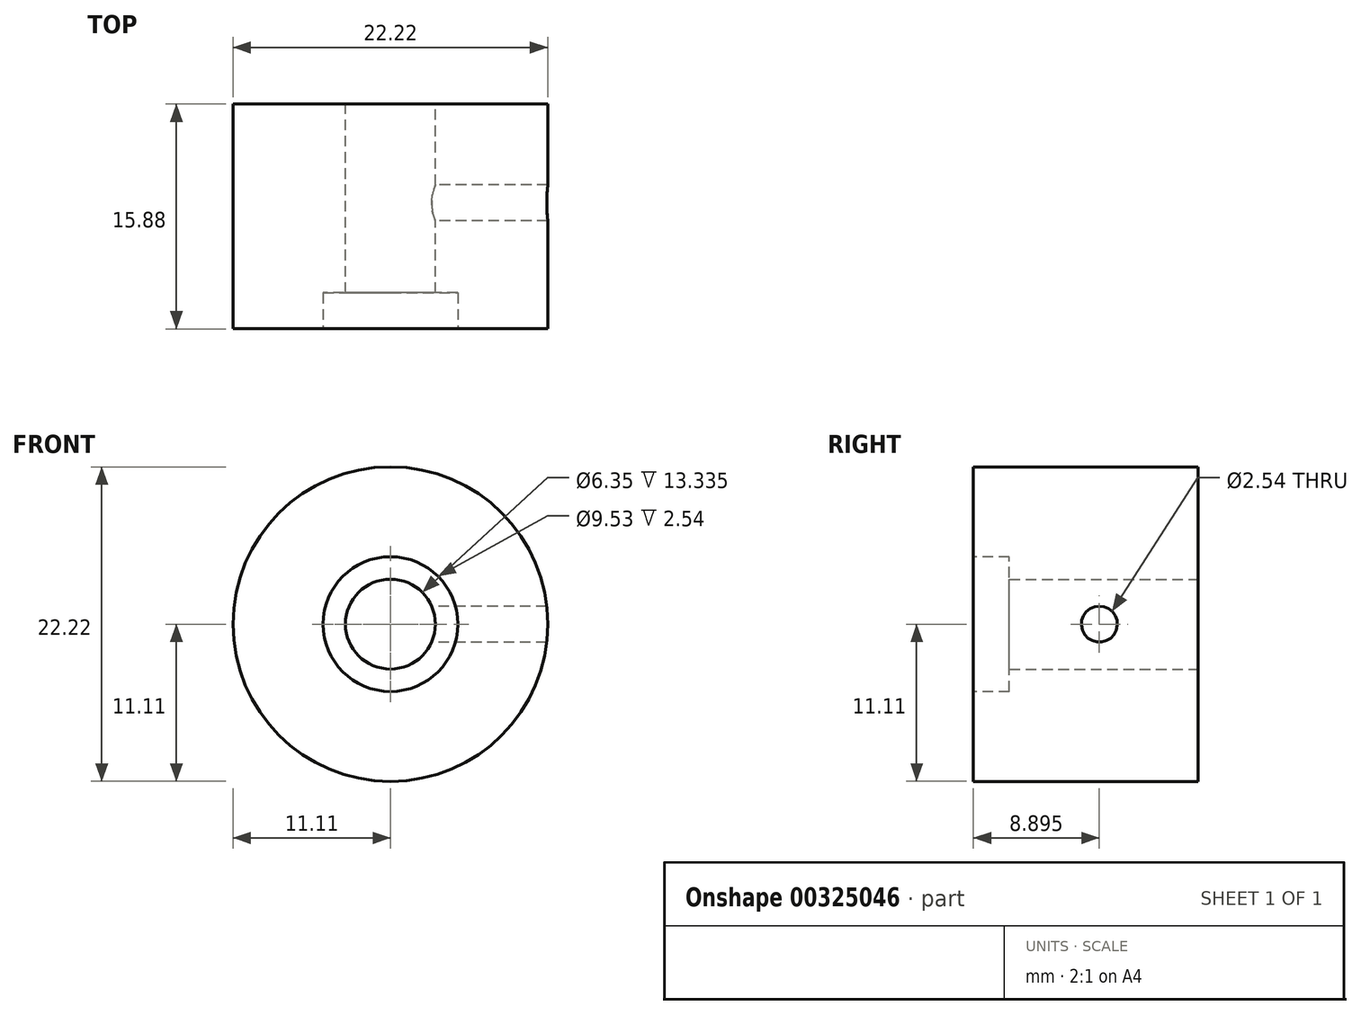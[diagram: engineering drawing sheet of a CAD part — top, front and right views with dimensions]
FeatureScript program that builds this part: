
annotation { "Feature Type Name" : "Feature", "Feature Type Description" : "" }
export const myFeature = defineFeature(function(context is Context, id is Id, definition is map)
    precondition{}
    {
        {
            var Q0;
            Q0=qCreatedBy(makeId("Front.planeOp"),FACE);
            var sketch = newSketch(context, id + "F0", { "sketchPlane" : qUnion([Q0])});
            skCircle(sketch, "E0", {"center": v(0, 0) * mm, "radius": 11.11 * mm});
            skCircle(sketch, "E1", {"center": v(0, 0) * mm, "radius": 3.18 * mm});
            skSolve(sketch);
        }
        {
            var Q0;
            Q0=makeQuery(id+"F0.imprint","IMPRINT",FACE,{"disambiguationData":[TD([[makeQuery(id+"F0.imprint","IMPRINT",EDGE,{"derivedFrom":sQuery(id+"F0.wireOp",EDGE,"E0")}),1.0]])]});
            extrude(context, id + "F1", {"entities" : qUnion([Q0]), "depth" : 15.88 * mm});
        }
        {
            var Q0;
            Q0=makeQuery(id+"F1.opExtrude","CAP_FACE",FACE,{"disambiguationData":[OSD([sQuery(id+"F0.wireOp",EDGE,"E0"),sQuery(id+"F0.wireOp",EDGE,"E1")])],"isStart":false});
            var sketch = newSketch(context, id + "F2", { "sketchPlane" : qUnion([Q0])});
            skCircle(sketch, "E2", {"center": v(0, 0) * mm, "radius": 4.76 * mm});
            skSolve(sketch);
        }
        {
            var Q0;
            Q0=makeQuery(id+"F2.imprint","IMPRINT",FACE,{"disambiguationData":[TD([[makeQuery(id+"F2.imprint","IMPRINT",EDGE,{"derivedFrom":sQuery(id+"F2.wireOp",EDGE,"E2")}),1.0]])]});
            extrude(context, id + "F3", {"entities" : qUnion([Q0]), "operationType" : NewBodyOperationType.REMOVE, "oppositeDirection" : true, "depth" : 2.54 * mm});
        }
        {
            var Q0;
            Q0=qCreatedBy(makeId("Right.planeOp"),FACE);
            var sketch = newSketch(context, id + "F4", { "sketchPlane" : qUnion([Q0])});
            skCircle(sketch, "E3", {"center": v(-6.99, 0) * mm, "radius": 1.27 * mm});
            skSolve(sketch);
        }
        {
            var Q0;
            Q0=makeQuery(id+"F4.imprint","IMPRINT",FACE,{"disambiguationData":[TD([[makeQuery(id+"F4.imprint","IMPRINT",EDGE,{"derivedFrom":sQuery(id+"F4.wireOp",EDGE,"E3")}),1.0]])]});
            var Q1;
            Q1=sQuery(id+"F4.wireOp",EDGE,"E3");
            extrude(context, id + "F5", {"entities" : qUnion([Q0]), "operationType" : NewBodyOperationType.REMOVE, "surfaceEntities" : qUnion([Q1]), "endBound" : BoundingType.THROUGH_ALL, "depth" : 25.4 * mm});
        }
    });
